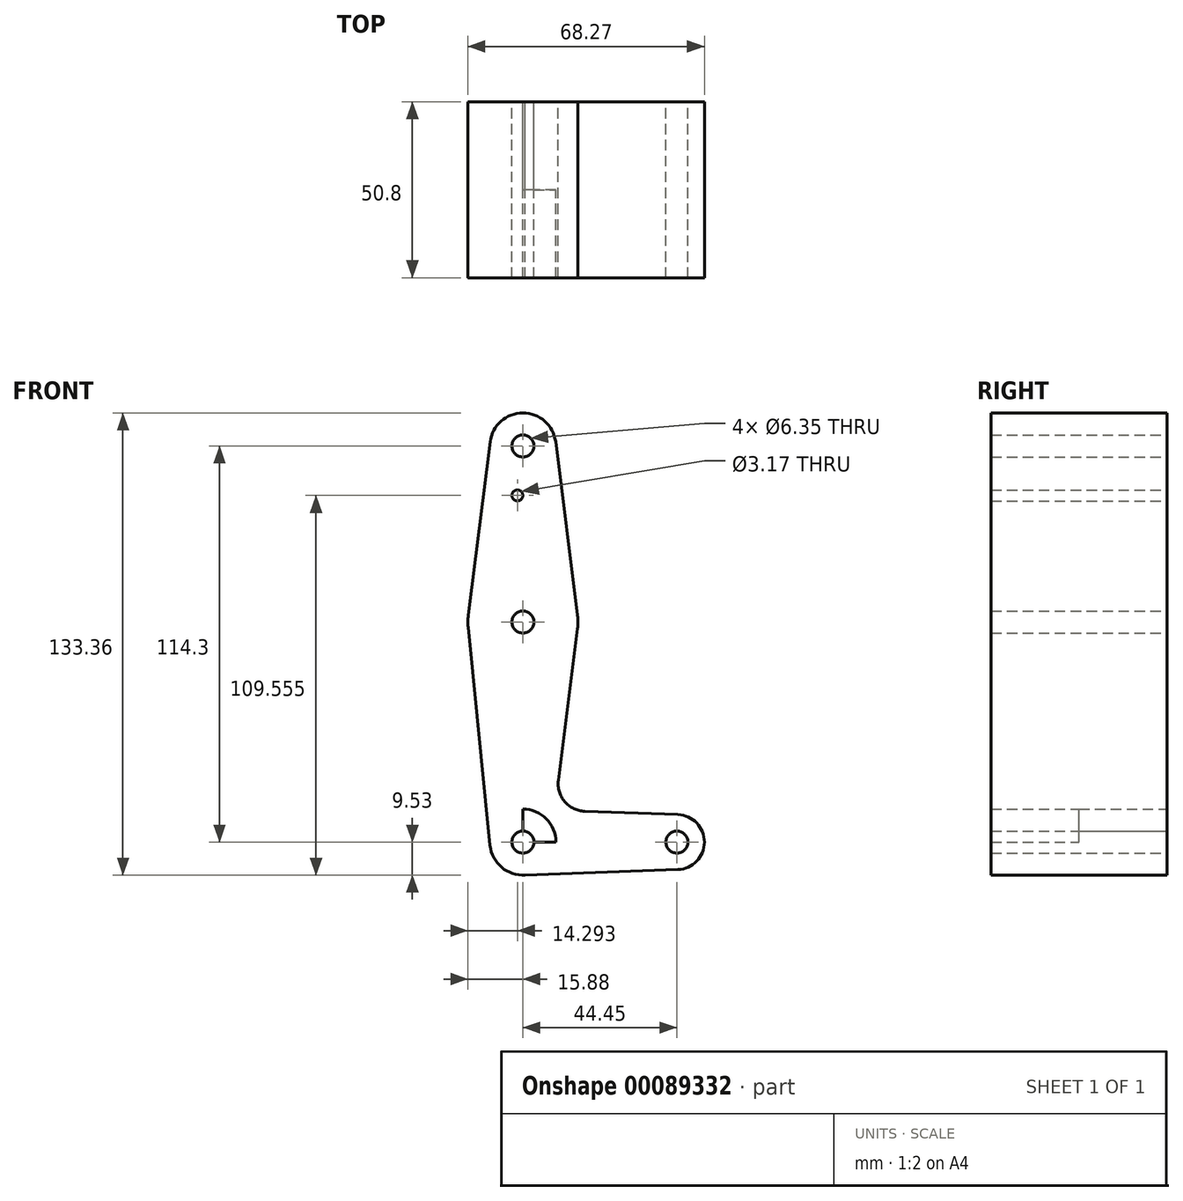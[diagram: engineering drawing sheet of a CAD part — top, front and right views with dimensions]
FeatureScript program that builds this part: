
annotation { "Feature Type Name" : "Feature", "Feature Type Description" : "" }
export const myFeature = defineFeature(function(context is Context, id is Id, definition is map)
    precondition{}
    {
        {
            var Q0;
            Q0=qCreatedBy(makeId("Front.planeOp"),FACE);
            var sketch = newSketch(context, id + "F0", { "sketchPlane" : qUnion([Q0])});
            skCircle(sketch, "E0", {"center": v(44.45, 0) * mm, "radius": 7.94 * mm});
            skCircle(sketch, "E1", {"center": v(0, 0) * mm, "radius": 9.53 * mm});
            skCircle(sketch, "E2", {"center": v(0, 63.5) * mm, "radius": 15.88 * mm});
            skCircle(sketch, "E3", {"center": v(0, 114.3) * mm, "radius": 9.53 * mm});
            skLineSegment(sketch, "E4", {"start": v(0, 0) * mm, "end": v(0, 63.5) * mm});
            skLineSegment(sketch, "E5", {"start": v(0, 0) * mm, "end": v(44.45, 0) * mm});
            skLineSegment(sketch, "E6", {"start": v(0, 63.5) * mm, "end": v(0, 114.3) * mm});
            skLineSegment(sketch, "E7", {"start": v(-15.75, 65.48) * mm, "end": v(-9.45, 115.5) * mm});
            skLineSegment(sketch, "E8", {"start": v(15.75, 65.48) * mm, "end": v(9.45, 115.5) * mm});
            skLineSegment(sketch, "E9", {"start": v(15.75, 61.52) * mm, "end": v(10.25, 17.83) * mm});
            skLineSegment(sketch, "E10", {"start": v(0, 9.52) * mm, "end": v(0.68, 9.5) * mm});
            skLineSegment(sketch, "E11", {"start": v(0, -9.53) * mm, "end": v(44.73, -7.93) * mm});
            skCircle(sketch, "E12", {"center": v(0, 114.3) * mm, "radius": 3.18 * mm});
            skCircle(sketch, "E13", {"center": v(0, 63.5) * mm, "radius": 3.18 * mm});
            skCircle(sketch, "E14", {"center": v(0, 0) * mm, "radius": 3.18 * mm});
            skCircle(sketch, "E15", {"center": v(44.45, 0) * mm, "radius": 3.18 * mm});
            skCircle(sketch, "E16", {"center": v(-1.59, 100.03) * mm, "radius": 1.59 * mm});
            skPoint(sketch, "E17.endSnap0", {"position": v(22.37, 8.73) * mm});
            skLineSegment(sketch, "E18.trimOffspring", {"start": v(17.85, 8.89) * mm, "end": v(44.73, 7.93) * mm});
            skArc(sketch, "E19", {"start": v(10.25, 17.83) * mm, "mid": v(12.08, 11.68) * mm, "end": v(17.85, 8.89) * mm});
            skLineSegment(sketch, "E20", {"start": v(-15.8, 61.91) * mm, "end": v(-9.48, -0.95) * mm});
            skSolve(sketch);
        }
        {
            var Q0;
            Q0 = qSketchRegion(id + "F0", true);
            extrude(context, id + "F1", {"entities" : qUnion([Q0]), "depth" : 3.05 * mm});
        }
        {
            var Q0;
            {var subQ0=sQuery(id+"F0.wireOp",EDGE,"E11");var subQ1=sQuery(id+"F0.wireOp",EDGE,"E1");var subQ2=makeQuery(id+"F0.imprint","INTERSECT",VERTEX,{"disambiguationData":[OD(0.0)],"derivedFrom":[subQ1,subQ0]});Q0=makeQuery(id+"F0.imprint","IMPRINT",FACE,{"disambiguationData":[TD([[makeQuery(id+"F0.imprint","IMPRINT",EDGE,{"disambiguationData":[TD([[subQ2,-1.0]])],"derivedFrom":subQ1}),1.0]])]});}
            var Q1;
            Q1=makeQuery(id+"F0.imprint","IMPRINT",FACE,{"disambiguationData":[TD([[makeQuery(id+"F0.imprint","IMPRINT",EDGE,{"derivedFrom":sQuery(id+"F0.wireOp",EDGE,"E15")}),-1.0]])]});
            var Q2;
            {var subQ0=sQuery(id+"F0.wireOp",EDGE,"E11");var subQ1=sQuery(id+"F0.wireOp",EDGE,"E0");var subQ2=makeQuery(id+"F0.imprint","INTERSECT",VERTEX,{"derivedFrom":[subQ1,subQ0]});Q2=makeQuery(id+"F0.imprint","IMPRINT",FACE,{"disambiguationData":[TD([[makeQuery(id+"F0.imprint","IMPRINT",EDGE,{"disambiguationData":[TD([[subQ2,1.0]])],"derivedFrom":subQ1}),-1.0]])]});}
            var Q3;
            {var subQ3=sQuery(id+"F0.wireOp",EDGE,"E20");Q3=makeQuery(id+"F0.imprint","IMPRINT",FACE,{"disambiguationData":[TD([[makeQuery(id+"F0.imprint","IMPRINT",EDGE,{"derivedFrom":subQ3}),1.0]])]});}
            var Q4;
            {var subQ4=sQuery(id+"F0.wireOp",EDGE,"E8");Q4=makeQuery(id+"F0.imprint","IMPRINT",FACE,{"disambiguationData":[TD([[makeQuery(id+"F0.imprint","IMPRINT",EDGE,{"derivedFrom":subQ4}),1.0]])]});}
            var Q5;
            Q5=makeQuery(id+"F0.imprint","IMPRINT",FACE,{"disambiguationData":[TD([[makeQuery(id+"F0.imprint","IMPRINT",EDGE,{"derivedFrom":sQuery(id+"F0.wireOp",EDGE,"E12")}),-1.0]])]});
            var Q6;
            {var subQ1=sQuery(id+"F0.wireOp",EDGE,"E2");var subQ5=makeQuery(id+"F0.imprint","INTERSECT",VERTEX,{"derivedFrom":[subQ1,sQuery(id+"F0.wireOp",EDGE,"E8")]});Q6=makeQuery(id+"F0.imprint","IMPRINT",FACE,{"disambiguationData":[TD([[makeQuery(id+"F0.imprint","IMPRINT",EDGE,{"disambiguationData":[TD([[subQ5,-1.0]])],"derivedFrom":subQ1}),1.0]])]});}
            var Q7;
            {var subQ1=sQuery(id+"F0.wireOp",EDGE,"E2");var subQ6=makeQuery(id+"F0.imprint","INTERSECT",VERTEX,{"derivedFrom":[subQ1,sQuery(id+"F0.wireOp",EDGE,"E7")]});Q7=makeQuery(id+"F0.imprint","IMPRINT",FACE,{"disambiguationData":[TD([[makeQuery(id+"F0.imprint","IMPRINT",EDGE,{"disambiguationData":[TD([[subQ6,1.0]])],"derivedFrom":subQ1}),1.0]])]});}
            var Q8;
            {var subQ7=sQuery(id+"F0.wireOp",EDGE,"E7");Q8=makeQuery(id+"F0.imprint","IMPRINT",FACE,{"disambiguationData":[TD([[makeQuery(id+"F0.imprint","IMPRINT",EDGE,{"derivedFrom":subQ7}),-1.0]])]});}
            var Q9;
            {var subQ0=sQuery(id+"F0.wireOp",EDGE,"E11");var subQ1=sQuery(id+"F0.wireOp",EDGE,"E1");var subQ9=makeQuery(id+"F0.imprint","INTERSECT",VERTEX,{"disambiguationData":[OD(0.0)],"derivedFrom":[subQ1,subQ0]});Q9=makeQuery(id+"F0.imprint","IMPRINT",FACE,{"disambiguationData":[TD([[makeQuery(id+"F0.imprint","IMPRINT",EDGE,{"disambiguationData":[TD([[subQ9,1.0]])],"derivedFrom":subQ1}),1.0]])]});}
            var Q10;
            {var subQ0=sQuery(id+"F0.wireOp",EDGE,"E9");Q10=makeQuery(id+"F0.imprint","IMPRINT",FACE,{"disambiguationData":[TD([[makeQuery(id+"F0.imprint","IMPRINT",EDGE,{"derivedFrom":subQ0}),-1.0]])]});}
            extrude(context, id + "F2", {"entities" : qUnion([Q0, Q1, Q2, Q3, Q4, Q5, Q6, Q7, Q8, Q9, Q10]), "operationType" : NewBodyOperationType.ADD, "depth" : 25.4 * mm});
        }
        {
            var Q0;
            Q0=makeQuery(id+"F2.opExtrude","CAP_FACE",FACE,{"disambiguationData":[OSD([sQuery(id+"F0.wireOp",EDGE,"E0"),sQuery(id+"F0.wireOp",EDGE,"E1"),sQuery(id+"F0.wireOp",EDGE,"E2"),sQuery(id+"F0.wireOp",EDGE,"E3"),sQuery(id+"F0.wireOp",EDGE,"E4"),sQuery(id+"F0.wireOp",EDGE,"E5"),sQuery(id+"F0.wireOp",EDGE,"E7"),sQuery(id+"F0.wireOp",EDGE,"E8"),sQuery(id+"F0.wireOp",EDGE,"E9"),sQuery(id+"F0.wireOp",EDGE,"E11"),sQuery(id+"F0.wireOp",EDGE,"E12"),sQuery(id+"F0.wireOp",EDGE,"E13"),sQuery(id+"F0.wireOp",EDGE,"E14"),sQuery(id+"F0.wireOp",EDGE,"E15"),sQuery(id+"F0.wireOp",EDGE,"E16"),sQuery(id+"F0.wireOp",EDGE,"E18.trimOffspring"),sQuery(id+"F0.wireOp",EDGE,"E19"),sQuery(id+"F0.wireOp",EDGE,"E20")])],"isStart":false});
            var Q1;
            {var subQ5=sQuery(id+"F0.wireOp",EDGE,"E10");Q1=makeQuery(id+"F0.imprint","IMPRINT",FACE,{"disambiguationData":[TD([[makeQuery(id+"F0.imprint","IMPRINT",EDGE,{"derivedFrom":subQ5}),-1.0]])]});}
            extrude(context, id + "F3", {"entities" : qUnion([Q0, Q1]), "operationType" : NewBodyOperationType.ADD, "depth" : 25.4 * mm});
        }
    });
